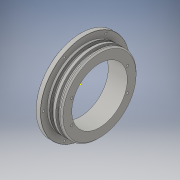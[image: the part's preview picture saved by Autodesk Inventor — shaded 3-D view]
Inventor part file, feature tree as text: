
AUTODESK INVENTOR PART (.ipt)
format: ipt  version: 2016 (Build 200138000, 138)  size: 450,048 bytes
history: native  units: in
note: dims shown in document units (in); Inventor stores cm internally (conversion verified against a paired STEP export)
features: sketch x5, extrude x3, chamfer x2, revolve x1, hole x1
ambient origin geometry x8: Origin, YZ Plane, XZ Plane, XY Plane, X Axis, Y Axis, Z Axis, Center Point
bodies: Solid1 (feature_tree)
feature tree (12):
  revolve  "Revolution1"  [1 undecoded]
  extrude  "Extrusion1"  Depth=0.13in
  extrude  "Extrusion2"  Depth=0.24in
  chamfer  "Chamfer1"  Distance=0.24in
  hole  "Hole1"  [1 undecoded]
  chamfer  "Chamfer2"  Distance=0.125in
  sketch  "Sketch8"  dims[d22=0.139in d23=0.0in d32=0.07in d33=0.125in d34=45.0deg]
  extrude  "Extrusion4"  Depth=0.995in
  sketch  "Sketch2"  dims[d2=0.175in d3=0.14in]
  sketch  "Sketch3"  dims[d4=0.175in d5=0.13in]
  sketch  "Sketch5"  dims[d8=90.0deg d10=4.65in d11=0.24in d12=0.0in]
  sketch  "Sketch9"  dims[d38=0.5in d42=0.125in d43=4.35in d44=2.3622in d46=360.0deg d48=0.1181in d49=0.75in d50=0.375in d51=0.25in d52=0.5635in d53=1.0in d54=0.8108in d55=0.01in d56=0.125in d57=45.0deg d62=3.819in d65=0.15in d66=0.15in d67=0.15in d68=0.055in d71=0.755in d72=1.68in d73=0.3in d74=0.3in d78=0.1181in d79=0.1181in d83=0.1181in d84=0.1181in d85=0.995in d86=0.0in]
note: 2 required parameter values undecoded (feature->parameter linkage not recoverable at this tier; creation-order binding heuristic only, values carry confidence <= 0.55)